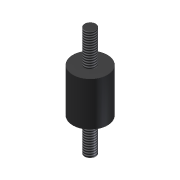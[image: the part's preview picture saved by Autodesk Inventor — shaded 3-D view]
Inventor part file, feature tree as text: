
AUTODESK INVENTOR PART (.ipt)
format: ipt  version: unknown  size: 181,248 bytes
history: native  units: mm (DEFAULTED — no unit token found)
features: extrude x2, thread x2, sketch x2
ambient origin geometry x8: Origin, YZ Plane, XZ Plane, XY Plane, X Axis, Y Axis, Z Axis, Center Point
feature tree (6):
  extrude  "Extrusion12"  Depth=10.0mm
  extrude  "Extrusion13"  Depth=31.75mm TaperAngle=0.0deg
  thread  "Thread1"  [1 undecoded]
  thread  "Thread2"  [1 undecoded]
  sketch  "Sketch19"  dims[d6=1.984375mm d87=10.0mm]
  sketch  "Sketch20"  dims[d89=12.7mm d90=0.0mm d91=31.75mm d92=0.0mm d93=3.175mm d94=10.0mm d95=0.0mm d96=10.0mm d97=0.0mm]
note: 2 required parameter values undecoded (feature->parameter linkage not recoverable at this tier; creation-order binding heuristic only, values carry confidence <= 0.55)
